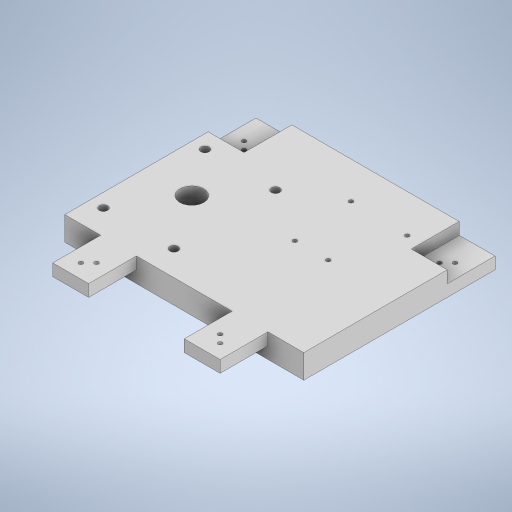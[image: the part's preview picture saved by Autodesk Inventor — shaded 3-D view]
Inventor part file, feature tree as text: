
AUTODESK INVENTOR PART (.ipt)
format: ipt  version: 2023 (Build 270158000, 158)  size: 339,968 bytes
history: native  units: mm
features: sketch x7, extrude x4, hole x3, other x1
ambient origin geometry x8: Origin, YZ Plane, XZ Plane, XY Plane, X Axis, Y Axis, Z Axis, Center Point
bodies: Body1 (feature_tree)
feature tree (15):
  other  "Sólido1"
  extrude  "Extrusión1"  Depth=160.0mm
  extrude  "Extrusión2"  Depth=30.0mm
  hole  "Agujero1"  [1 undecoded]
  extrude  "Extrusión3"  Depth=11.75mm
  hole  "Agujero2"  [1 undecoded]
  hole  "Agujero3"  [1 undecoded]
  extrude  "Extrusión4"  Depth=40.0mm TaperAngle=0.0deg
  sketch  "Boceto1"  dims[d0=200.0mm d1=160.0mm]
  sketch  "Boceto2"  dims[d2=20.0mm d3=0.0mm d4=30.0mm]
  sketch  "Boceto3"  dims[d5=40.0mm d6=10.0mm d7=0.0mm]
  sketch  "Boceto4"  dims[d23=21.75mm d24=11.75mm]
  sketch  "Boceto5"  dims[d26=11.75mm]
  sketch  "Boceto6"  dims[d27=3.5mm d28=6.0mm d29=4.0mm d30=2.0mm d31=90.0deg d32=8.0mm d33=20.594885mm d34=30.0mm]
  sketch  "Boceto7"  dims[d35=10.0mm d36=30.0mm d37=40.0mm d38=0.0mm d39=10.0mm d40=10.0mm d41=40.0mm d42=0.0mm d43=6.5mm d44=6.5mm d45=3.5mm d46=3.5mm d47=11.749873mm d48=11.75mm d49=0.0mm d50=11.75mm d51=0.0mm d52=3.5mm d53=6.0mm d54=4.0mm d55=2.0mm d56=90.0deg d57=8.0mm d58=20.594885mm d59=7.0mm d60=7.0mm d61=7.0mm d62=39.0mm d63=46.0mm d64=59.0mm d65=46.0mm d66=39.0mm d67=59.0mm d68=52.0mm d69=70.0mm d70=22.0mm d71=42.0mm d72=3.5mm d73=3.5mm d74=3.5mm d75=3.5mm d76=3.5mm d77=6.0mm d78=4.0mm d79=2.0mm d80=90.0deg d81=8.0mm d82=20.594885mm d83=7.0mm d84=7.0mm d85=7.0mm d86=39.0mm d87=46.0mm d88=59.0mm d89=46.0mm d90=39.0mm d91=59.0mm d92=20.0mm d93=0.0mm d94=1.0mm d95=0.15mm d96=0.25mm d97=0.375mm d98=14.3117mm d99=0.75mm d100=20.594885mm d101=0.0625mm d102=0.75mm d103=0.375mm]
note: 3 required parameter values undecoded (feature->parameter linkage not recoverable at this tier; creation-order binding heuristic only, values carry confidence <= 0.55)
